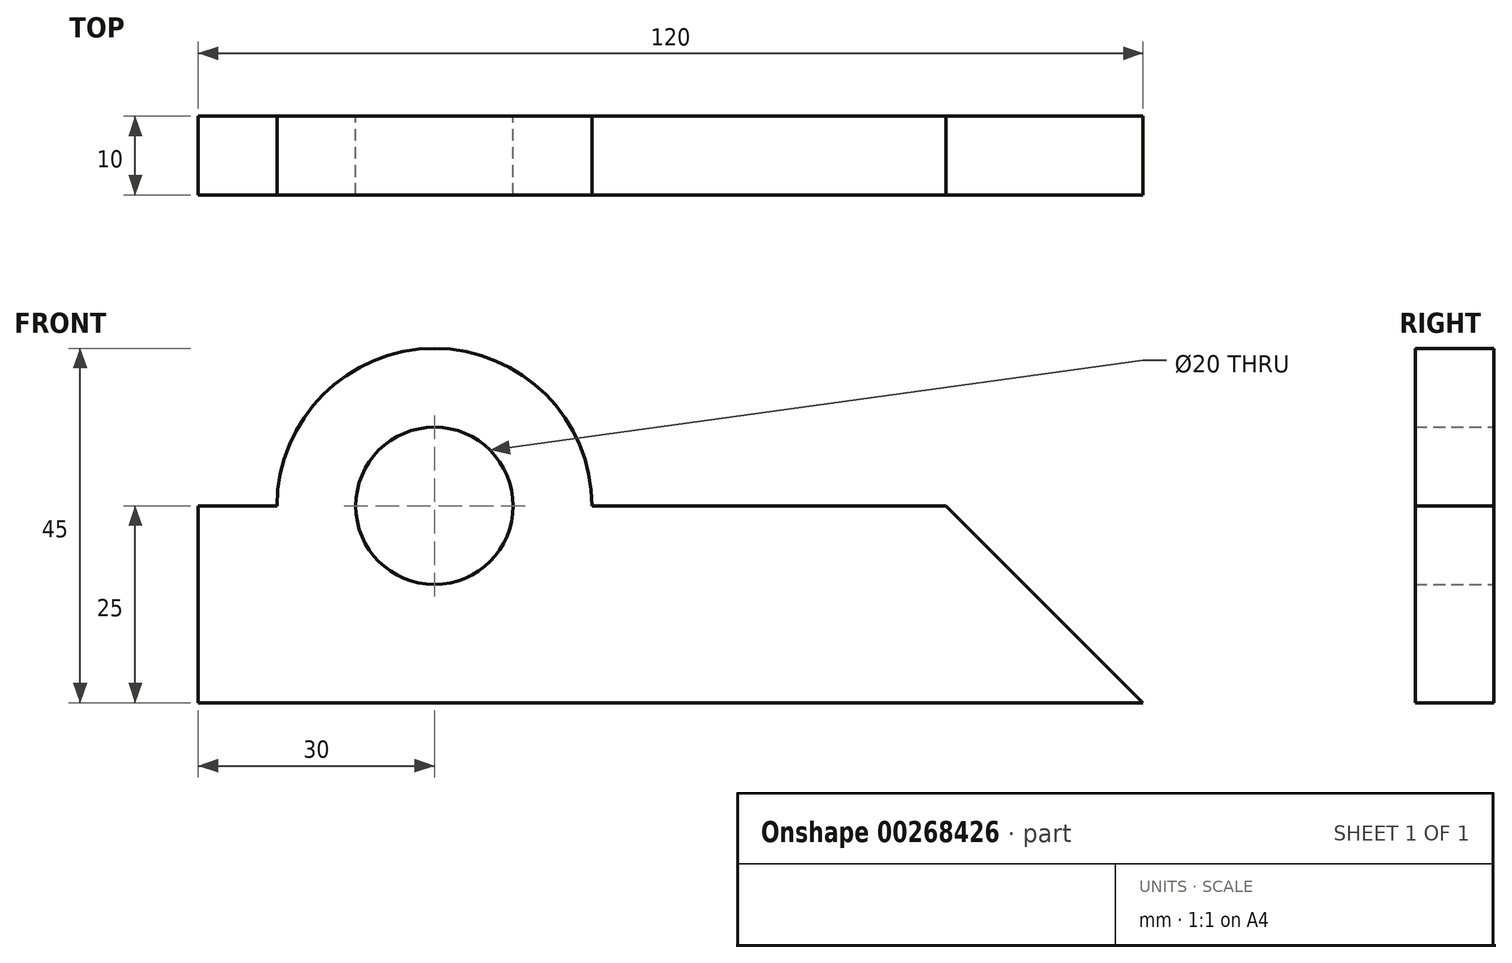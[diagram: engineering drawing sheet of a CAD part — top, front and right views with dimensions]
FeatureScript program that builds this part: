
annotation { "Feature Type Name" : "Feature", "Feature Type Description" : "" }
export const myFeature = defineFeature(function(context is Context, id is Id, definition is map)
    precondition{}
    {
        {
            var Q0;
            Q0=qCreatedBy(makeId("Front.planeOp"),FACE);
            var sketch = newSketch(context, id + "F0", { "sketchPlane" : qUnion([Q0])});
            skLineSegment(sketch, "E0", {"start": v(0, 0) * mm, "end": v(120, 0) * mm});
            skLineSegment(sketch, "E1", {"start": v(0, 0) * mm, "end": v(0, 25) * mm});
            skLineSegment(sketch, "E2", {"start": v(120, 0) * mm, "end": v(95, 25) * mm});
            skLineSegment(sketch, "E3", {"start": v(95, 25) * mm, "end": v(50, 25) * mm});
            skLineSegment(sketch, "E4", {"start": v(0, 25) * mm, "end": v(10, 25) * mm});
            skArc(sketch, "E5", {"start": v(50, 25) * mm, "mid": v(30, 45) * mm, "end": v(10, 25) * mm});
            skCircle(sketch, "E6", {"center": v(30, 25) * mm, "radius": 10 * mm});
            skSolve(sketch);
        }
        {
            var Q0;
            Q0 = qSketchRegion(id + "F0", true);
            extrude(context, id + "F1", {"entities" : qUnion([Q0]), "depth" : 10 * mm});
        }
    });
